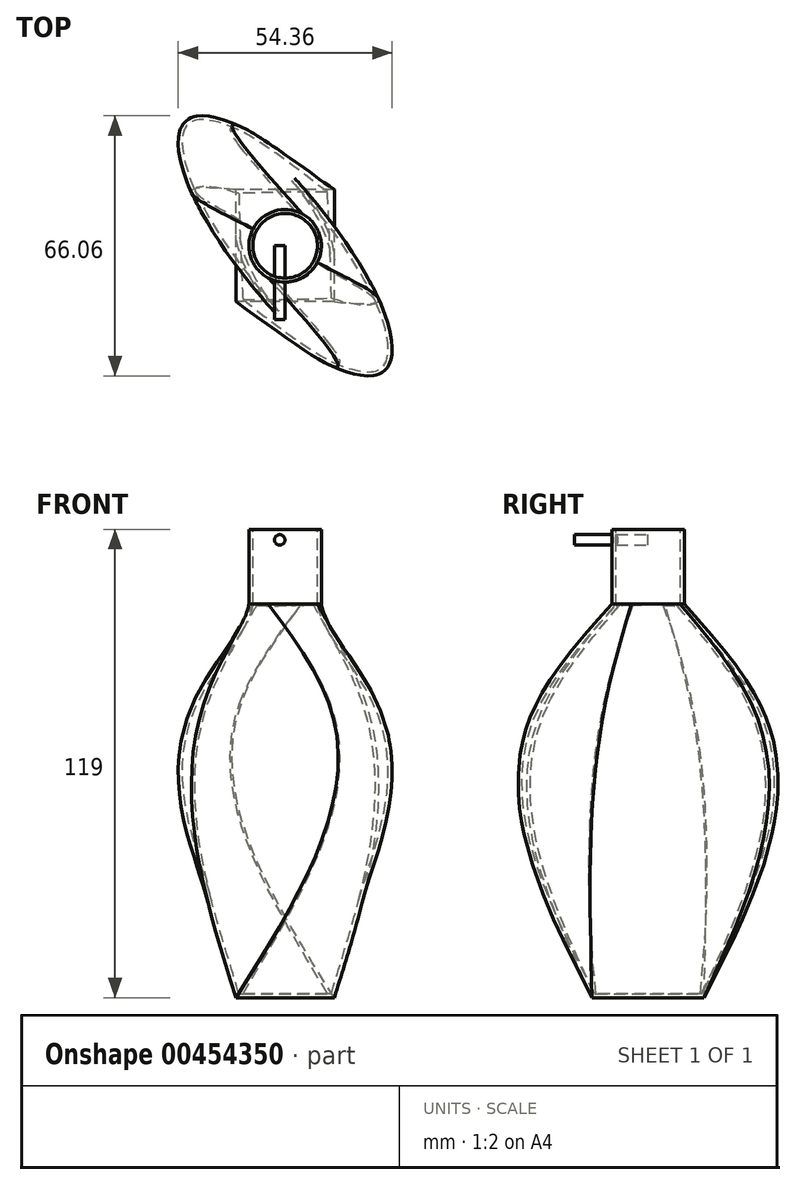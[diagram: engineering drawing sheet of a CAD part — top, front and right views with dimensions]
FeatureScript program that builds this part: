
annotation { "Feature Type Name" : "Feature", "Feature Type Description" : "" }
export const myFeature = defineFeature(function(context is Context, id is Id, definition is map)
    precondition{}
    {
        {
            var Q0;
            Q0=qCreatedBy(makeId("Top.planeOp"),FACE);
            var sketch = newSketch(context, id + "F0", { "sketchPlane" : qUnion([Q0])});
            skLineSegment(sketch, "E0.bottom", {"start": v(12.5, -14.22) * mm, "end": v(-12.5, -14.22) * mm});
            skLineSegment(sketch, "E0.top", {"start": v(12.5, 14.22) * mm, "end": v(-12.5, 14.22) * mm});
            skLineSegment(sketch, "E0.left", {"start": v(12.5, -14.22) * mm, "end": v(12.5, 14.22) * mm});
            skLineSegment(sketch, "E0.right", {"start": v(-12.5, -14.22) * mm, "end": v(-12.5, 14.22) * mm});
            skPoint(sketch, "E0.middle", {"position": v(0, 0) * mm});
            skSolve(sketch);
        }
        {
            var Q0;
            Q0=qCreatedBy(makeId("Top.planeOp"),FACE);
            cPlane(context, id + "F1", {"entities" : qUnion([Q0]), "cplaneType" : CPlaneType.OFFSET, "offset" : 75 * mm, "width" : 150 * mm, "height" : 150 * mm});
        }
        {
            var Q0;
            Q0=qCreatedBy(id+"F1.planeOp",FACE);
            var sketch = newSketch(context, id + "F2", { "sketchPlane" : qUnion([Q0])});
            skEllipse(sketch, "E1", {"center": v(0, 0) * mm, "majorRadius": 34.62 * mm, "minorRadius": 12.05 * mm, "majorAxis": v(0.62, -0.79)});
            skSolve(sketch);
        }
        {
            var Q0;
            Q0=qCreatedBy(id+"F1.planeOp",FACE);
            cPlane(context, id + "F3", {"entities" : qUnion([Q0]), "cplaneType" : CPlaneType.OFFSET, "offset" : 25 * mm, "width" : 150 * mm, "height" : 150 * mm});
        }
        {
            var Q0;
            Q0=qCreatedBy(id+"F3.planeOp",FACE);
            var sketch = newSketch(context, id + "F4", { "sketchPlane" : qUnion([Q0])});
            skCircle(sketch, "E2", {"center": v(0, 0) * mm, "radius": 9.2 * mm});
            skSolve(sketch);
        }
        {
            var Q0;
            Q0=makeQuery(id+"F0.imprint","IMPRINT",FACE,{"disambiguationData":[TD([[makeQuery(id+"F0.imprint","IMPRINT",EDGE,{"derivedFrom":sQuery(id+"F0.wireOp",EDGE,"E0.bottom")}),-1.0]])]});
            var Q1;
            Q1=makeQuery(id+"F2.imprint","IMPRINT",FACE,{"disambiguationData":[TD([[makeQuery(id+"F2.imprint","IMPRINT",EDGE,{"derivedFrom":sQuery(id+"F2.wireOp",EDGE,"E1")}),1.0]])]});
            var Q2;
            Q2=makeQuery(id+"F4.imprint","IMPRINT",FACE,{"disambiguationData":[TD([[makeQuery(id+"F4.imprint","IMPRINT",EDGE,{"derivedFrom":sQuery(id+"F4.wireOp",EDGE,"E2")}),1.0]])]});
            loft(context, id + "F5", {"sheetProfilesArray" : [{ "sheetProfileEntities" : qUnion([Q0]) }, { "sheetProfileEntities" : qUnion([Q1]) }, { "sheetProfileEntities" : qUnion([Q2]) }]});
        }
        {
            var Q0;
            Q0=makeQuery(id+"F5.opLoft","CAP_FACE",FACE,{"disambiguationData":[OSD([makeQuery(id+"F4.imprint","IMPRINT",FACE,{"disambiguationData":[TD([[makeQuery(id+"F4.imprint","IMPRINT",EDGE,{"derivedFrom":sQuery(id+"F4.wireOp",EDGE,"E2")}),1.0]])]})])],"isStart":true});
            extrude(context, id + "F6", {"entities" : qUnion([Q0]), "operationType" : NewBodyOperationType.ADD, "depth" : 19 * mm});
        }
        {
            var Q0;
            Q0=makeQuery(id+"F6.opExtrude","CAP_FACE",FACE,{"disambiguationData":[OSD([makeQuery(id+"F4.imprint","IMPRINT",FACE,{"disambiguationData":[TD([[makeQuery(id+"F4.imprint","IMPRINT",EDGE,{"derivedFrom":sQuery(id+"F4.wireOp",EDGE,"E2")}),1.0]])]})])],"isStart":false});
            shell(context, id + "F7", {"entities" : qUnion([Q0]), "thickness" : 1 * mm});
        }
        {
            var Q0;
            Q0=qCreatedBy(makeId("Front.planeOp"),FACE);
            var sketch = newSketch(context, id + "F8", { "sketchPlane" : qUnion([Q0])});
            skCircle(sketch, "E3", {"center": v(-1.36, 116.31) * mm, "radius": 1.32 * mm});
            skSolve(sketch);
        }
        {
            var Q0;
            Q0=makeQuery(id+"F8.imprint","IMPRINT",FACE,{"disambiguationData":[TD([[makeQuery(id+"F8.imprint","IMPRINT",EDGE,{"derivedFrom":sQuery(id+"F8.wireOp",EDGE,"E3")}),1.0]])]});
            extrude(context, id + "F9", {"entities" : qUnion([Q0]), "operationType" : NewBodyOperationType.ADD, "depth" : 18.76 * mm});
        }
    });
